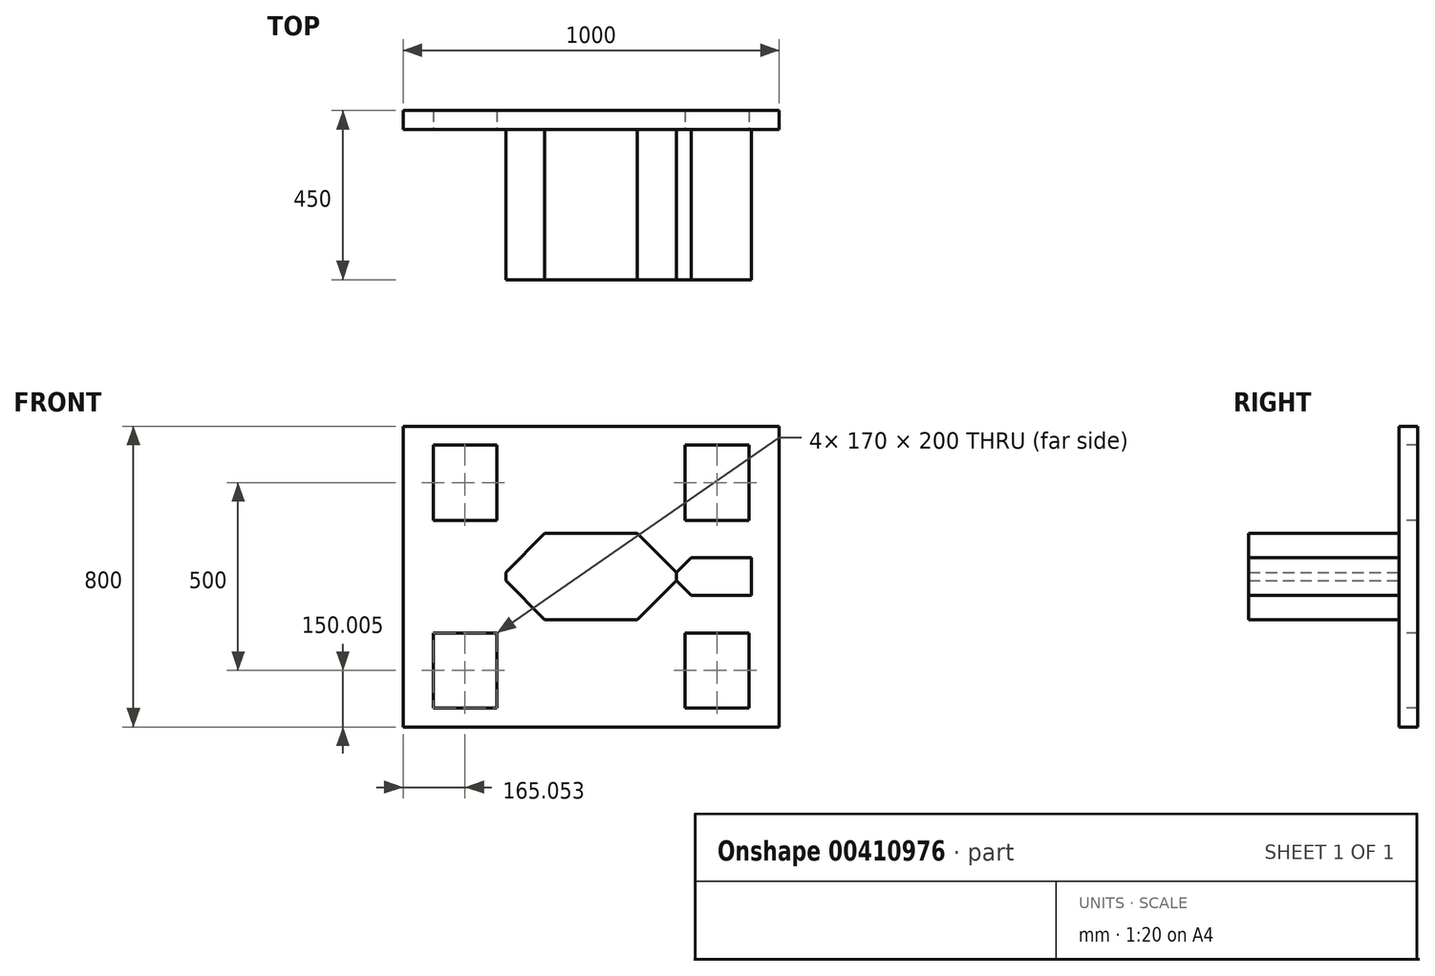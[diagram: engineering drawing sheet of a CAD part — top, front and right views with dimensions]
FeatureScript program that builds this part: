
annotation { "Feature Type Name" : "Feature", "Feature Type Description" : "" }
export const myFeature = defineFeature(function(context is Context, id is Id, definition is map)
    precondition{}
    {
        {
            var Q0;
            Q0=qCreatedBy(makeId("Front.planeOp"),FACE);
            var sketch = newSketch(context, id + "F0", { "sketchPlane" : qUnion([Q0])});
            skLineSegment(sketch, "E0", {"start": v(-245.96, 0.09) * mm, "end": v(-350, 104.56) * mm});
            skLineSegment(sketch, "E1", {"start": v(-350, 104.56) * mm, "end": v(-350, 125.56) * mm});
            skLineSegment(sketch, "E2", {"start": v(-350, 125.56) * mm, "end": v(-246, 230.09) * mm});
            skLineSegment(sketch, "E3", {"start": v(-246, 230.09) * mm, "end": v(0, 230.09) * mm});
            skLineSegment(sketch, "E4", {"start": v(0, 230.09) * mm, "end": v(104, 125.56) * mm});
            skLineSegment(sketch, "E5", {"start": v(104, 125.56) * mm, "end": v(104, 104.56) * mm});
            skLineSegment(sketch, "E6", {"start": v(104, 104.56) * mm, "end": v(0.04, 0) * mm});
            skLineSegment(sketch, "E7", {"start": v(0.04, 0) * mm, "end": v(-245.96, 0.09) * mm});
            skLineSegment(sketch, "E8", {"start": v(161.51, 115.06) * mm, "end": v(-374.8, 115.06) * mm, "construction": true});
            skPoint(sketch, "E8.startSnap0", {"position": v(104, 115.06) * mm});
            skPoint(sketch, "E8.endSnap0", {"position": v(-350, 115.06) * mm});
            skPoint(sketch, "E9.endSnap0", {"position": v(-122.96, 0.04) * mm});
            skLineSegment(sketch, "E10", {"start": v(-122.96, -71.87) * mm, "end": v(-122.96, 249.58) * mm, "construction": true});
            skPoint(sketch, "E11", {"position": v(-122.96, 115.06) * mm});
            skSolve(sketch);
        }
        {
            var Q0;
            Q0=makeQuery(id+"F0.imprint","IMPRINT",FACE,{"disambiguationData":[TD([[makeQuery(id+"F0.imprint","IMPRINT",EDGE,{"derivedFrom":sQuery(id+"F0.wireOp",EDGE,"E0")}),-1.0]])]});
            extrude(context, id + "F1", {"entities" : qUnion([Q0]), "depth" : 400 * mm});
        }
        {
            var Q0;
            Q0=makeQuery(id+"F1.opExtrude","CAP_FACE",FACE,{"disambiguationData":[OSD([sQuery(id+"F0.wireOp",EDGE,"E0"),sQuery(id+"F0.wireOp",EDGE,"E1"),sQuery(id+"F0.wireOp",EDGE,"E2"),sQuery(id+"F0.wireOp",EDGE,"E3"),sQuery(id+"F0.wireOp",EDGE,"E4"),sQuery(id+"F0.wireOp",EDGE,"E5"),sQuery(id+"F0.wireOp",EDGE,"E6"),sQuery(id+"F0.wireOp",EDGE,"E7")])],"isStart":true});
            var sketch = newSketch(context, id + "F2", { "sketchPlane" : qUnion([Q0])});
            skLineSegment(sketch, "E12.bottom", {"start": v(-376.99, 515.06) * mm, "end": v(623.01, 515.06) * mm});
            skLineSegment(sketch, "E12.top", {"start": v(-376.99, -284.94) * mm, "end": v(623.01, -284.94) * mm});
            skLineSegment(sketch, "E12.left", {"start": v(-376.99, 515.06) * mm, "end": v(-376.99, -284.94) * mm});
            skLineSegment(sketch, "E12.right", {"start": v(623.01, 515.06) * mm, "end": v(623.01, -284.94) * mm});
            skLineSegment(sketch, "E13", {"start": v(122.96, -124.83) * mm, "end": v(123.01, 327.76) * mm, "construction": true});
            skPoint(sketch, "E13.startSnap0", {"position": v(122.96, 0.04) * mm});
            skLineSegment(sketch, "E14", {"start": v(-146.45, 115.06) * mm, "end": v(416.01, 115.06) * mm, "construction": true});
            skPoint(sketch, "E14.startSnap0", {"position": v(-104, 115.06) * mm});
            skSolve(sketch);
        }
        {
            var Q0;
            Q0=qSketchRegion(id+"F2",true);
            extrude(context, id + "F3", {"entities" : qUnion([Q0]), "depth" : 50 * mm});
        }
        {
            var Q0;
            Q0=makeQuery(id+"F3.opExtrude","CAP_FACE",FACE,{"disambiguationData":[OSD([sQuery(id+"F2.wireOp",EDGE,"E12.bottom"),sQuery(id+"F2.wireOp",EDGE,"E12.top"),sQuery(id+"F2.wireOp",EDGE,"E12.left"),sQuery(id+"F2.wireOp",EDGE,"E12.right")])],"isStart":true});
            var sketch = newSketch(context, id + "F4", { "sketchPlane" : qUnion([Q0])});
            skLineSegment(sketch, "E15.bottom", {"start": v(-542.96, 265.06) * mm, "end": v(-372.96, 265.06) * mm});
            skLineSegment(sketch, "E15.top", {"start": v(-542.96, 465.06) * mm, "end": v(-372.96, 465.06) * mm});
            skLineSegment(sketch, "E15.left", {"start": v(-542.96, 265.06) * mm, "end": v(-542.96, 465.06) * mm});
            skLineSegment(sketch, "E15.right", {"start": v(-372.96, 265.06) * mm, "end": v(-372.96, 465.06) * mm});
            skPoint(sketch, "E16.0", {"position": v(-122.96, 0.04) * mm});
            skPoint(sketch, "E17.0", {"position": v(-123, 230.09) * mm});
            skPoint(sketch, "E18.0", {"position": v(-350, 115.06) * mm});
            skPoint(sketch, "E19.0", {"position": v(104, 115.06) * mm});
            skLineSegment(sketch, "E20", {"start": v(-122.96, -129.88) * mm, "end": v(-122.96, 413.53) * mm, "construction": true});
            skLineSegment(sketch, "E21", {"start": v(180.49, 115.06) * mm, "end": v(-440.47, 115.06) * mm, "construction": true});
            skLineSegment(sketch, "E22.MirrorCS", {"start": v(127.04, 265.06) * mm, "end": v(127.04, 465.06) * mm});
            skLineSegment(sketch, "E23.MirrorCS", {"start": v(297.04, 265.06) * mm, "end": v(127.04, 265.06) * mm});
            skLineSegment(sketch, "E24.MirrorCS", {"start": v(297.04, 265.06) * mm, "end": v(297.04, 465.06) * mm});
            skLineSegment(sketch, "E25.MirrorCS", {"start": v(297.04, 465.06) * mm, "end": v(127.04, 465.06) * mm});
            skLineSegment(sketch, "E26.MirrorCS", {"start": v(-542.96, -34.94) * mm, "end": v(-372.96, -34.94) * mm});
            skLineSegment(sketch, "E27.MirrorCS", {"start": v(-542.96, -34.94) * mm, "end": v(-542.96, -234.94) * mm});
            skLineSegment(sketch, "E28.MirrorCS", {"start": v(-542.96, -234.94) * mm, "end": v(-372.96, -234.94) * mm});
            skLineSegment(sketch, "E29.MirrorCS", {"start": v(-372.96, -34.94) * mm, "end": v(-372.96, -234.94) * mm});
            skLineSegment(sketch, "E30.MirrorCS", {"start": v(127.04, -34.94) * mm, "end": v(127.04, -234.94) * mm});
            skLineSegment(sketch, "E31.MirrorCS", {"start": v(297.04, -234.94) * mm, "end": v(127.04, -234.94) * mm});
            skLineSegment(sketch, "E32.MirrorCS", {"start": v(297.04, -34.94) * mm, "end": v(297.04, -234.94) * mm});
            skLineSegment(sketch, "E33.MirrorCS", {"start": v(297.04, -34.94) * mm, "end": v(127.04, -34.94) * mm});
            skSolve(sketch);
        }
        {
            var Q0;
            Q0=makeQuery(id+"F1.opExtrude","CAP_FACE",FACE,{"disambiguationData":[OSD([sQuery(id+"F0.wireOp",EDGE,"E0"),sQuery(id+"F0.wireOp",EDGE,"E1"),sQuery(id+"F0.wireOp",EDGE,"E2"),sQuery(id+"F0.wireOp",EDGE,"E3"),sQuery(id+"F0.wireOp",EDGE,"E4"),sQuery(id+"F0.wireOp",EDGE,"E5"),sQuery(id+"F0.wireOp",EDGE,"E6"),sQuery(id+"F0.wireOp",EDGE,"E7")])],"isStart":false});
            var sketch = newSketch(context, id + "F5", { "sketchPlane" : qUnion([Q0])});
            skLineSegment(sketch, "E34", {"start": v(-350, 115.06) * mm, "end": v(319.5, 115.06) * mm, "construction": true});
            skLineSegment(sketch, "E35", {"start": v(-122.96, -187.75) * mm, "end": v(-123, 464.97) * mm, "construction": true});
            skPoint(sketch, "E35.startSnap0", {"position": v(-122.96, 0.04) * mm});
            skPoint(sketch, "E35.endSnap0", {"position": v(-123, 230.09) * mm});
            skSolve(sketch);
        }
        {
            var Q0;
            Q0=makeQuery(id+"F4.imprint","IMPRINT",FACE,{"disambiguationData":[TD([[makeQuery(id+"F4.imprint","IMPRINT",EDGE,{"derivedFrom":sQuery(id+"F4.wireOp",EDGE,"E26.MirrorCS")}),-1.0]])]});
            var Q1;
            Q1=makeQuery(id+"F4.imprint","IMPRINT",FACE,{"disambiguationData":[TD([[makeQuery(id+"F4.imprint","IMPRINT",EDGE,{"derivedFrom":sQuery(id+"F4.wireOp",EDGE,"E15.bottom")}),1.0]])]});
            var Q2;
            Q2=makeQuery(id+"F4.imprint","IMPRINT",FACE,{"disambiguationData":[TD([[makeQuery(id+"F4.imprint","IMPRINT",EDGE,{"derivedFrom":sQuery(id+"F4.wireOp",EDGE,"E22.MirrorCS")}),-1.0]])]});
            var Q3;
            Q3=makeQuery(id+"F4.imprint","IMPRINT",FACE,{"disambiguationData":[TD([[makeQuery(id+"F4.imprint","IMPRINT",EDGE,{"derivedFrom":sQuery(id+"F4.wireOp",EDGE,"E30.MirrorCS")}),1.0]])]});
            extrude(context, id + "F6", {"entities" : qUnion([Q0, Q1, Q2, Q3]), "operationType" : NewBodyOperationType.REMOVE, "endBound" : BoundingType.UP_TO_NEXT, "oppositeDirection" : true, "depth" : 25 * mm});
        }
        {
            var Q0;
            Q0=makeQuery(id+"F5.imprint","IMPRINT",FACE,{"disambiguationData":[TD([[makeQuery(id+"F5.imprint","IMPRINT",EDGE,{"derivedFrom":makeQuery(id+"F1.opExtrude","CAP_EDGE",EDGE,{"disambiguationData":[OSD([sQuery(id+"F0.wireOp",EDGE,"E0")])],"isStart":false})}),-1.0]])]});
            var sketch = newSketch(context, id + "F7", { "sketchPlane" : qUnion([Q0])});
            skLineSegment(sketch, "E36.0", {"start": v(104, 115.06) * mm, "end": v(104, 104.56) * mm});
            skLineSegment(sketch, "E37.0", {"start": v(-350, 115.06) * mm, "end": v(319.5, 115.06) * mm, "construction": true});
            skLineSegment(sketch, "E38", {"start": v(104, 104.56) * mm, "end": v(143.73, 65.06) * mm});
            skLineSegment(sketch, "E39", {"start": v(143.73, 65.06) * mm, "end": v(304, 65.06) * mm});
            skLineSegment(sketch, "E40", {"start": v(304, 65.06) * mm, "end": v(304, 115.06) * mm});
            skLineSegment(sketch, "E41.MirrorCS", {"start": v(304, 165.06) * mm, "end": v(304, 115.06) * mm});
            skLineSegment(sketch, "E42.MirrorCS", {"start": v(143.73, 165.06) * mm, "end": v(304, 165.06) * mm});
            skLineSegment(sketch, "E43.MirrorCS", {"start": v(104, 125.56) * mm, "end": v(143.73, 165.06) * mm});
            skLineSegment(sketch, "E44.MirrorCS", {"start": v(104, 115.06) * mm, "end": v(104, 125.56) * mm});
            skSolve(sketch);
        }
        {
            var Q0;
            Q0=makeQuery(id+"F7.imprint","IMPRINT",FACE,{"disambiguationData":[TD([[makeQuery(id+"F7.imprint","IMPRINT",EDGE,{"derivedFrom":sQuery(id+"F7.wireOp",EDGE,"E36.0")}),1.0]])]});
            extrude(context, id + "F8", {"entities" : qUnion([Q0]), "oppositeDirection" : true, "depth" : 400 * mm});
        }
    });
